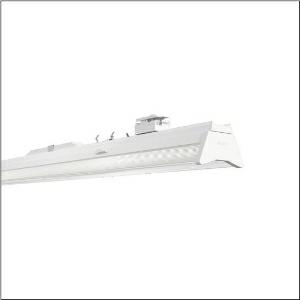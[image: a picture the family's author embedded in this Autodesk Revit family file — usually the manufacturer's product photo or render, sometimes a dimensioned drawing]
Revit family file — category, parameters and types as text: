
# Revit family: licross_r__21_performance_mo_52tm167n445g_e37c
name_source: partatom
category: Lighting Fixtures
units: mm (PartAtom-declared; Revit-internal decimal feet)

## family parameters
Cut with Voids When Loaded = No
Host = Face
Light Source = No
Part Type = Normal
Room Calculation Point = No
Round Connector Dimension = Use Diameter
Shared = No

## types (1)
- Licross® 21 Performance MO (1 x LED, 4580 lm, 24.7 W, 4000K)
    Apparent Load = 25 VA
    CIE Flux Codes = 66 88 96 79 100
    Color Rendering = 80
    Color Temperature = 4000K
    Default Elevation = 1800 mm
    Description = Licross® 21 Performance MO, luminaire insert, of sheet steel, galvanised, coil coated, white, length: 1.500mm, width: 120mm, height: 123mm, LED rated luminous flux: 4.580lm, light colour: 840, control gear: ON/OFF, with plug, 3-pole, with phase selection, mains connection: 220..240V, AC, 50/60Hz, rated input power: 25W, internal wiring halogen-free, primary light control with lens, of plastic, primary optical cover: cover, of PMMA, CAT 2 (L<= 3000cd/m²), light emission: direct/indirect distribution, primary light characteristic: symmetric, protection rating (complete): IP40, insulation class (complete): insulation class I (protective earthing), certification: CE, ENEC, UKCA, protection symbol: D if used in an environment without relevant dust loads with corresponding accessories, impact resistance: IK06, permissible ambient temperature for indoor applications: -35..+55°C, corresponds to IFS (International Featured Standards) requirements for safety and quality in the food industry, reducing of maximum allowable ambient temperature of 5°C with ceiling mounting, LABS conformity tested according to VDMA 24364:2018-05, packaging unit: 1 piece
    Height = 114 mm
    Lamp = 1 x LED
    Lamp Light Flux = 4580 lm
    Lamp Power = 24.7 W
    Lamp count = 1
    Length = 1500 mm
    Luminous efficacy = 185 lm/W
    Manufacturer = Siteco
    ModVariant = No
    Model = 52TM167N445G
    Mounting Place = Ceiling
    Mounting Type = Pendant
    Number of Poles = 1
    OnlyDefault = Yes
    Power Factor = 1
    Product Name = Licross® 21 Performance MO
    Product group = luminaire insert | ceiling pendant
    ProductGroupID = 902
    Protection Class = Protection class I
    Protection Degree = IP 40
    RLX_Detail_Level = 1
    RLX_Emergency_Light_Flux = 0 lm
    RLX_Emergency_Type = 0
    RLX_Emergency_Type_DB = No
    RlxData = <blob elided: 30505 chars, md5=201bf943>
    Socket = socket
    Standby Power = 0 W
    System Light Flux = 4580 lm
    System Power = 25 W
    Type Comments = Product without accessories
    Type Image = l_1256138.jpg
    URL = http://relux.com
    VarID = ---
    Voltage = 0 V
    Weight = 0.00 kg
    Width = 120 mm

## geometry (parser evidence)
native form markers: Blend x4, Sweep x10
no freeform markers — native parametric forms only
